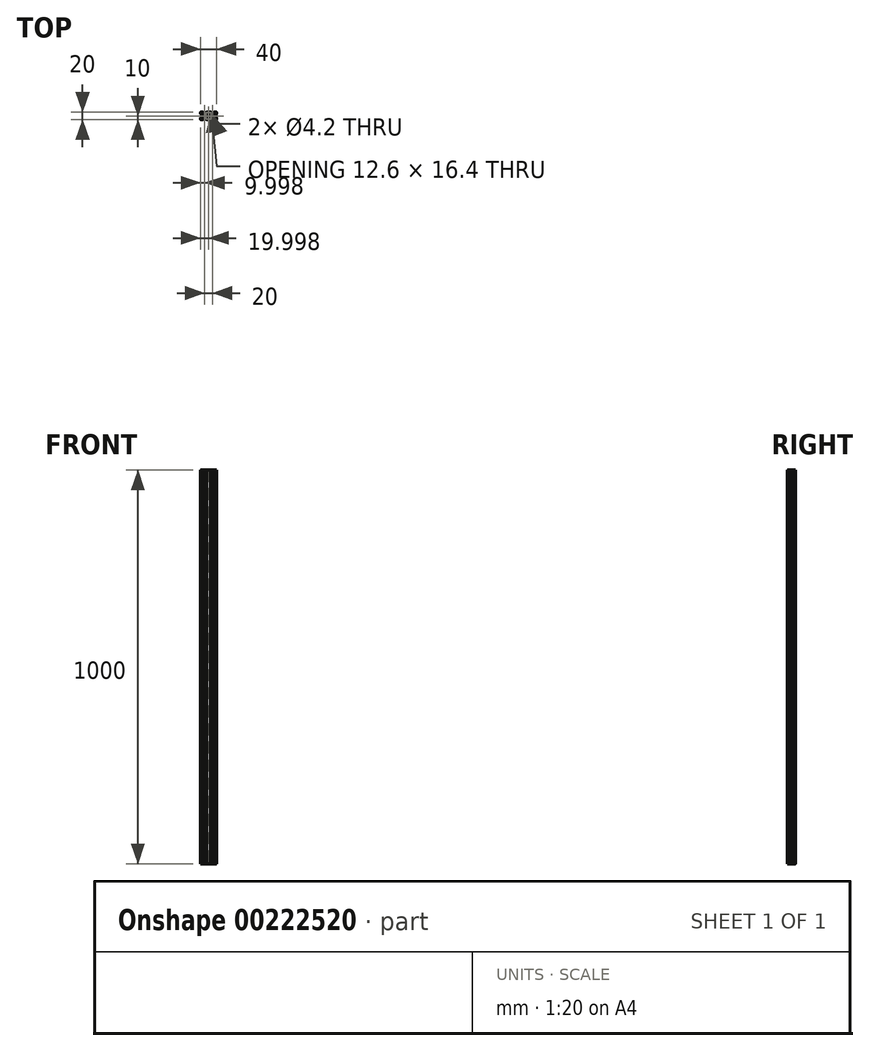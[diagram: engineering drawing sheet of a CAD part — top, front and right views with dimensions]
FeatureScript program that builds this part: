
annotation { "Feature Type Name" : "Feature", "Feature Type Description" : "" }
export const myFeature = defineFeature(function(context is Context, id is Id, definition is map)
    precondition{}
    {
        {
            var Q0;
            Q0=qCreatedBy(makeId("Top.planeOp"),FACE);
            var sketch = newSketch(context, id + "F0", { "sketchPlane" : qUnion([Q0])});
            skLineSegment(sketch, "E0", {"start": v(-2.86, 5.2) * mm, "end": v(-2.86, 3.09) * mm});
            skLineSegment(sketch, "E1", {"start": v(-2.86, -3.09) * mm, "end": v(-2.86, -5.2) * mm});
            skCircle(sketch, "E2", {"center": v(5.34, 0) * mm, "radius": 2.1 * mm});
            skLineSegment(sketch, "E3", {"start": v(5.24, -3.9) * mm, "end": v(5.34, -3.7) * mm});
            skArc(sketch, "E4", {"start": v(1.35, -2.93) * mm, "mid": v(1.41, -2.83) * mm, "end": v(1.44, -2.72) * mm});
            skLineSegment(sketch, "E5", {"start": v(5.44, -3.9) * mm, "end": v(5.34, -3.7) * mm});
            skArc(sketch, "E6", {"start": v(22.41, 3.99) * mm, "mid": v(22.5, 3.92) * mm, "end": v(22.62, 3.9) * mm});
            skCircle(sketch, "E7", {"center": v(25.34, 0) * mm, "radius": 2.1 * mm});
            skArc(sketch, "E8", {"start": v(28.05, 3.9) * mm, "mid": v(28.17, 3.92) * mm, "end": v(28.27, 3.99) * mm});
            skArc(sketch, "E9", {"start": v(22.62, -3.9) * mm, "mid": v(22.5, -3.92) * mm, "end": v(22.41, -3.99) * mm});
            skArc(sketch, "E10", {"start": v(28.27, -3.99) * mm, "mid": v(28.17, -3.92) * mm, "end": v(28.05, -3.9) * mm});
            skArc(sketch, "E11", {"start": v(29.24, -2.72) * mm, "mid": v(29.26, -2.83) * mm, "end": v(29.33, -2.93) * mm});
            skLineSegment(sketch, "E12", {"start": v(29.33, -2.93) * mm, "end": v(31.9, -5.5) * mm});
            skLineSegment(sketch, "E13", {"start": v(31.9, -5.5) * mm, "end": v(33.24, -5.5) * mm});
            skArc(sketch, "E14", {"start": v(33.24, -5.5) * mm, "mid": v(33.45, -5.41) * mm, "end": v(33.54, -5.2) * mm});
            skArc(sketch, "E15", {"start": v(30.54, -8.2) * mm, "mid": v(30.75, -8.11) * mm, "end": v(30.84, -7.9) * mm});
            skLineSegment(sketch, "E16", {"start": v(28.27, -3.99) * mm, "end": v(30.84, -6.56) * mm});
            skLineSegment(sketch, "E17", {"start": v(30.84, -6.56) * mm, "end": v(30.84, -7.9) * mm});
            skLineSegment(sketch, "E18", {"start": v(29.24, 2.72) * mm, "end": v(29.24, 0.1) * mm});
            skLineSegment(sketch, "E19", {"start": v(29.24, 0.1) * mm, "end": v(29.04, 0) * mm});
            skLineSegment(sketch, "E20", {"start": v(29.04, 0) * mm, "end": v(29.24, -0.1) * mm});
            skLineSegment(sketch, "E21", {"start": v(29.24, -0.1) * mm, "end": v(29.24, -2.72) * mm});
            skArc(sketch, "E22", {"start": v(29.33, 2.93) * mm, "mid": v(29.26, 2.83) * mm, "end": v(29.24, 2.72) * mm});
            skLineSegment(sketch, "E23", {"start": v(29.33, 2.93) * mm, "end": v(31.9, 5.5) * mm});
            skLineSegment(sketch, "E24", {"start": v(31.9, 5.5) * mm, "end": v(33.24, 5.5) * mm});
            skArc(sketch, "E25", {"start": v(33.54, 5.2) * mm, "mid": v(33.45, 5.41) * mm, "end": v(33.24, 5.5) * mm});
            skLineSegment(sketch, "E26", {"start": v(28.27, 3.99) * mm, "end": v(30.84, 6.56) * mm});
            skLineSegment(sketch, "E27", {"start": v(30.84, 6.56) * mm, "end": v(30.84, 7.9) * mm});
            skArc(sketch, "E28", {"start": v(30.84, 7.9) * mm, "mid": v(30.75, 8.11) * mm, "end": v(30.54, 8.2) * mm});
            skLineSegment(sketch, "E29", {"start": v(22.62, 3.9) * mm, "end": v(25.24, 3.9) * mm});
            skLineSegment(sketch, "E30", {"start": v(25.24, 3.9) * mm, "end": v(25.34, 3.7) * mm});
            skLineSegment(sketch, "E31", {"start": v(25.34, 3.7) * mm, "end": v(25.44, 3.9) * mm});
            skLineSegment(sketch, "E32", {"start": v(25.44, 3.9) * mm, "end": v(28.05, 3.9) * mm});
            skArc(sketch, "E33", {"start": v(20.14, 8.2) * mm, "mid": v(19.93, 8.11) * mm, "end": v(19.84, 7.9) * mm});
            skLineSegment(sketch, "E34", {"start": v(20.45, 10) * mm, "end": v(10.23, 10) * mm});
            skLineSegment(sketch, "E35", {"start": v(10.23, 10) * mm, "end": v(8.42, 8.2) * mm});
            skLineSegment(sketch, "E36", {"start": v(22.41, 3.99) * mm, "end": v(19.84, 6.56) * mm});
            skLineSegment(sketch, "E37", {"start": v(19.84, 6.56) * mm, "end": v(19.84, 7.9) * mm});
            skLineSegment(sketch, "E38", {"start": v(2.62, 3.9) * mm, "end": v(5.24, 3.9) * mm});
            skLineSegment(sketch, "E39", {"start": v(5.24, 3.9) * mm, "end": v(5.34, 3.7) * mm});
            skLineSegment(sketch, "E40", {"start": v(5.34, 3.7) * mm, "end": v(5.44, 3.9) * mm});
            skLineSegment(sketch, "E41", {"start": v(5.44, 3.9) * mm, "end": v(8.05, 3.9) * mm});
            skArc(sketch, "E42", {"start": v(8.05, 3.9) * mm, "mid": v(8.17, 3.92) * mm, "end": v(8.27, 3.99) * mm});
            skLineSegment(sketch, "E43", {"start": v(8.27, 3.99) * mm, "end": v(10.84, 6.56) * mm});
            skLineSegment(sketch, "E44", {"start": v(10.84, 6.56) * mm, "end": v(10.84, 7.9) * mm});
            skLineSegment(sketch, "E45", {"start": v(1.44, -2.72) * mm, "end": v(1.44, -0.1) * mm});
            skLineSegment(sketch, "E46", {"start": v(1.44, -0.1) * mm, "end": v(1.64, 0) * mm});
            skLineSegment(sketch, "E47", {"start": v(1.64, 0) * mm, "end": v(1.44, 0.1) * mm});
            skLineSegment(sketch, "E48", {"start": v(1.44, 0.1) * mm, "end": v(1.44, 2.72) * mm});
            skArc(sketch, "E49", {"start": v(1.44, 2.72) * mm, "mid": v(1.41, 2.83) * mm, "end": v(1.35, 2.93) * mm});
            skLineSegment(sketch, "E50", {"start": v(1.35, 2.93) * mm, "end": v(-1.22, 5.5) * mm});
            skLineSegment(sketch, "E51", {"start": v(2.25, 8.2) * mm, "end": v(0.45, 10) * mm});
            skLineSegment(sketch, "E52", {"start": v(-4.66, 4.89) * mm, "end": v(-2.86, 3.09) * mm});
            skArc(sketch, "E53", {"start": v(-2.56, 5.5) * mm, "mid": v(-2.77, 5.41) * mm, "end": v(-2.86, 5.2) * mm});
            skLineSegment(sketch, "E54", {"start": v(-2.56, 5.5) * mm, "end": v(-1.22, 5.5) * mm});
            skArc(sketch, "E55", {"start": v(2.41, 3.99) * mm, "mid": v(2.5, 3.92) * mm, "end": v(2.62, 3.9) * mm});
            skLineSegment(sketch, "E56", {"start": v(2.41, 3.99) * mm, "end": v(-0.16, 6.56) * mm});
            skLineSegment(sketch, "E57", {"start": v(-0.16, 6.56) * mm, "end": v(-0.16, 7.9) * mm});
            skArc(sketch, "E58", {"start": v(0.14, 8.2) * mm, "mid": v(-0.07, 8.11) * mm, "end": v(-0.16, 7.9) * mm});
            skLineSegment(sketch, "E59", {"start": v(0.14, 8.2) * mm, "end": v(2.25, 8.2) * mm});
            skLineSegment(sketch, "E60", {"start": v(8.42, 8.2) * mm, "end": v(10.54, 8.2) * mm});
            skArc(sketch, "E61", {"start": v(10.84, 7.9) * mm, "mid": v(10.75, 8.11) * mm, "end": v(10.54, 8.2) * mm});
            skLineSegment(sketch, "E62", {"start": v(-2.86, -3.09) * mm, "end": v(-4.66, -4.89) * mm});
            skArc(sketch, "E63", {"start": v(-2.86, -5.2) * mm, "mid": v(-2.77, -5.41) * mm, "end": v(-2.56, -5.5) * mm});
            skLineSegment(sketch, "E64", {"start": v(-2.56, -5.5) * mm, "end": v(-1.22, -5.5) * mm});
            skLineSegment(sketch, "E65", {"start": v(-1.22, -5.5) * mm, "end": v(1.35, -2.93) * mm});
            skLineSegment(sketch, "E66", {"start": v(-0.16, -6.56) * mm, "end": v(-0.16, -7.9) * mm});
            skArc(sketch, "E67", {"start": v(-0.16, -7.9) * mm, "mid": v(-0.07, -8.11) * mm, "end": v(0.14, -8.2) * mm});
            skLineSegment(sketch, "E68", {"start": v(0.45, -10) * mm, "end": v(-4.26, -10) * mm});
            skLineSegment(sketch, "E69", {"start": v(5.24, -3.9) * mm, "end": v(2.62, -3.9) * mm});
            skArc(sketch, "E70", {"start": v(2.62, -3.9) * mm, "mid": v(2.5, -3.92) * mm, "end": v(2.41, -3.99) * mm});
            skLineSegment(sketch, "E71", {"start": v(2.41, -3.99) * mm, "end": v(-0.16, -6.56) * mm});
            skLineSegment(sketch, "E72", {"start": v(5.44, -3.9) * mm, "end": v(8.05, -3.9) * mm});
            skArc(sketch, "E73", {"start": v(8.05, -3.9) * mm, "mid": v(8.17, -3.92) * mm, "end": v(8.27, -3.99) * mm});
            skLineSegment(sketch, "E74", {"start": v(8.27, -3.99) * mm, "end": v(10.84, -6.56) * mm});
            skLineSegment(sketch, "E75", {"start": v(10.84, -6.56) * mm, "end": v(10.84, -7.9) * mm});
            skArc(sketch, "E76", {"start": v(19.84, -7.9) * mm, "mid": v(19.93, -8.11) * mm, "end": v(20.14, -8.2) * mm});
            skLineSegment(sketch, "E77", {"start": v(20.45, -10) * mm, "end": v(10.23, -10) * mm});
            skArc(sketch, "E78", {"start": v(10.54, -8.2) * mm, "mid": v(10.75, -8.11) * mm, "end": v(10.84, -7.9) * mm});
            skLineSegment(sketch, "E79", {"start": v(22.41, -3.99) * mm, "end": v(19.84, -6.56) * mm});
            skLineSegment(sketch, "E80", {"start": v(19.84, -6.56) * mm, "end": v(19.84, -7.9) * mm});
            skLineSegment(sketch, "E81", {"start": v(22.62, -3.9) * mm, "end": v(25.24, -3.9) * mm});
            skLineSegment(sketch, "E82", {"start": v(25.24, -3.9) * mm, "end": v(25.34, -3.7) * mm});
            skLineSegment(sketch, "E83", {"start": v(25.34, -3.7) * mm, "end": v(25.44, -3.9) * mm});
            skLineSegment(sketch, "E84", {"start": v(25.44, -3.9) * mm, "end": v(28.05, -3.9) * mm});
            skLineSegment(sketch, "E85", {"start": v(-4.66, -4.89) * mm, "end": v(-4.66, -9.6) * mm});
            skArc(sketch, "E86", {"start": v(-4.66, -9.6) * mm, "mid": v(-4.54, -9.88) * mm, "end": v(-4.26, -10) * mm});
            skLineSegment(sketch, "E87", {"start": v(0.45, 10) * mm, "end": v(-4.26, 10) * mm});
            skLineSegment(sketch, "E88", {"start": v(-4.66, 4.89) * mm, "end": v(-4.66, 9.6) * mm});
            skArc(sketch, "E89", {"start": v(-4.26, 10) * mm, "mid": v(-4.54, 9.88) * mm, "end": v(-4.66, 9.6) * mm});
            skLineSegment(sketch, "E90", {"start": v(30.23, -10) * mm, "end": v(34.94, -10) * mm});
            skLineSegment(sketch, "E91", {"start": v(35.34, -4.89) * mm, "end": v(35.34, -9.6) * mm});
            skArc(sketch, "E92", {"start": v(34.94, -10) * mm, "mid": v(35.22, -9.88) * mm, "end": v(35.34, -9.6) * mm});
            skLineSegment(sketch, "E93", {"start": v(30.23, 10) * mm, "end": v(34.94, 10) * mm});
            skLineSegment(sketch, "E94", {"start": v(35.34, 4.89) * mm, "end": v(35.34, 9.6) * mm});
            skArc(sketch, "E95", {"start": v(35.34, 9.6) * mm, "mid": v(35.22, 9.88) * mm, "end": v(34.94, 10) * mm});
            skLineSegment(sketch, "E96", {"start": v(10.23, -10) * mm, "end": v(8.42, -8.2) * mm});
            skLineSegment(sketch, "E97", {"start": v(2.25, -8.2) * mm, "end": v(0.45, -10) * mm});
            skLineSegment(sketch, "E98", {"start": v(0.14, -8.2) * mm, "end": v(2.25, -8.2) * mm});
            skLineSegment(sketch, "E99", {"start": v(8.42, -8.2) * mm, "end": v(10.54, -8.2) * mm});
            skLineSegment(sketch, "E100", {"start": v(33.54, 5.2) * mm, "end": v(33.54, 3.09) * mm});
            skLineSegment(sketch, "E101", {"start": v(33.54, -3.09) * mm, "end": v(33.54, -5.2) * mm});
            skLineSegment(sketch, "E102", {"start": v(20.45, 10) * mm, "end": v(22.25, 8.2) * mm});
            skLineSegment(sketch, "E103", {"start": v(28.42, 8.2) * mm, "end": v(30.23, 10) * mm});
            skLineSegment(sketch, "E104", {"start": v(35.34, 4.89) * mm, "end": v(33.54, 3.09) * mm});
            skLineSegment(sketch, "E105", {"start": v(30.54, 8.2) * mm, "end": v(28.42, 8.2) * mm});
            skLineSegment(sketch, "E106", {"start": v(22.25, 8.2) * mm, "end": v(20.14, 8.2) * mm});
            skLineSegment(sketch, "E107", {"start": v(33.54, -3.09) * mm, "end": v(35.34, -4.89) * mm});
            skLineSegment(sketch, "E108", {"start": v(20.45, -10) * mm, "end": v(22.25, -8.2) * mm});
            skLineSegment(sketch, "E109", {"start": v(28.42, -8.2) * mm, "end": v(30.23, -10) * mm});
            skLineSegment(sketch, "E110", {"start": v(30.54, -8.2) * mm, "end": v(28.42, -8.2) * mm});
            skLineSegment(sketch, "E111", {"start": v(22.25, -8.2) * mm, "end": v(20.14, -8.2) * mm});
            skLineSegment(sketch, "E112", {"start": v(12.64, 8.2) * mm, "end": v(18.04, 8.2) * mm});
            skLineSegment(sketch, "E113", {"start": v(18.04, 8.2) * mm, "end": v(18.04, 6.24) * mm});
            skLineSegment(sketch, "E114", {"start": v(18.04, 6.24) * mm, "end": v(21.35, 2.93) * mm});
            skLineSegment(sketch, "E115", {"start": v(21.35, 2.93) * mm, "end": v(21.44, 2.72) * mm});
            skLineSegment(sketch, "E116", {"start": v(21.44, 2.72) * mm, "end": v(21.44, 0.1) * mm});
            skLineSegment(sketch, "E117", {"start": v(21.44, 0.1) * mm, "end": v(21.64, 0) * mm});
            skLineSegment(sketch, "E118", {"start": v(21.64, 0) * mm, "end": v(21.44, -0.1) * mm});
            skLineSegment(sketch, "E119", {"start": v(21.44, -0.1) * mm, "end": v(21.44, -2.72) * mm});
            skLineSegment(sketch, "E120", {"start": v(21.44, -2.72) * mm, "end": v(21.27, -3) * mm});
            skLineSegment(sketch, "E121", {"start": v(21.27, -3) * mm, "end": v(18.04, -6.24) * mm});
            skLineSegment(sketch, "E122", {"start": v(18.04, -6.24) * mm, "end": v(18.04, -8.2) * mm});
            skLineSegment(sketch, "E123", {"start": v(18.04, -8.2) * mm, "end": v(12.64, -8.2) * mm});
            skLineSegment(sketch, "E124", {"start": v(12.64, -8.2) * mm, "end": v(12.64, -6.24) * mm});
            skLineSegment(sketch, "E125", {"start": v(12.64, -6.24) * mm, "end": v(9.33, -2.93) * mm});
            skLineSegment(sketch, "E126", {"start": v(9.33, -2.93) * mm, "end": v(9.24, -2.72) * mm});
            skLineSegment(sketch, "E127", {"start": v(9.24, -2.72) * mm, "end": v(9.24, -0.1) * mm});
            skLineSegment(sketch, "E128", {"start": v(9.24, -0.1) * mm, "end": v(9.04, 0) * mm});
            skLineSegment(sketch, "E129", {"start": v(9.04, 0) * mm, "end": v(9.24, 0.1) * mm});
            skLineSegment(sketch, "E130", {"start": v(9.24, 0.1) * mm, "end": v(9.24, 2.72) * mm});
            skLineSegment(sketch, "E131", {"start": v(9.24, 2.72) * mm, "end": v(9.33, 2.93) * mm});
            skLineSegment(sketch, "E132", {"start": v(9.33, 2.93) * mm, "end": v(12.64, 6.24) * mm});
            skLineSegment(sketch, "E133", {"start": v(12.64, 6.24) * mm, "end": v(12.64, 8.2) * mm});
            skSolve(sketch);
        }
        {
            var Q0;
            Q0 = qSketchRegion(id + "F0", true);
            extrude(context, id + "F1", {"entities" : qUnion([Q0]), "depth" : 1000 * mm});
        }
    });
